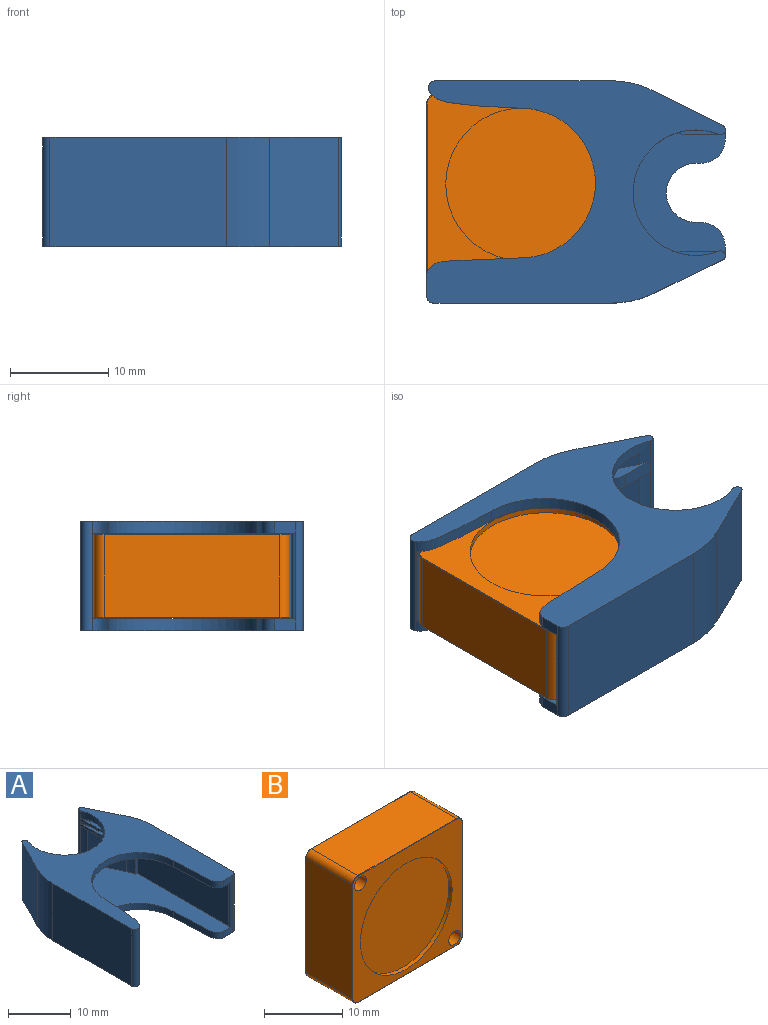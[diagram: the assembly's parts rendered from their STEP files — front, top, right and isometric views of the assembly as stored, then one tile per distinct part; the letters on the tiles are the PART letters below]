
ASSEMBLY  parts=2 mates=1
PART A: 64 faces, bbox 22.6x30.4x11.1 mm
  f0: plane 6.9x5.9mm, normal (-0.9,-0.44,0), area 45.2mm2, adj f2,f9,f31,f49
  f1: plane 5.9x2.86mm, normal (-0.9,-0.44,0), area 2mm2, adj f5,f15,f31,f55
  f2: cylinder r=6.38mm len=6.9mm, axis (0,0,1), area 8.8mm2, adj f0,f9,f42,f49
  f3: cylinder r=6.38mm len=1.23mm, axis (0,0,1), area 0.6mm2, adj f30,f42,f51,f53
  f4: plane 5.94x2.98mm, normal (0.89,-0.45,0), area 8.6mm2, adj f5,f15,f32,f47
  f5: cylinder r=6.38mm len=12.75mm, axis (0,0,1), area 31.7mm2, adj f1,f4,f8,f15,f40,f42,f47,f55
  f6: plane 2.16x1.2mm, normal (0,-1,0), area 2.6mm2, adj f8,f15,f24,f43
  f7: plane 1.2x0.88mm, normal (0,1,0), area 1.1mm2, adj f9,f10,f38,f39
  f8: plane 30.35x22.6mm, normal (0,0,1), area 298.4mm2, adj f5,f6,f18,f19,f21,f22,f24,f25
  f9: plane 30.35x20.76mm, normal (0,0,1), area 291.2mm2, adj f0,f2,f7,f11,f12,f13,f14,f16
  f10: plane 30.35x22.6mm, normal (0,0,-1), area 364.4mm2, adj f7,f11,f16,f18,f19,f20,f22,f23
  f11: plane 1.2x0.88mm, normal (0,1,0), area 1.1mm2, adj f9,f10,f37,f41
  f12: plane 8.7x0.32mm, normal (0,-1,0), area 2.8mm2, adj f9,f14,f15,f32
  f13: plane 8.7x0.3mm, normal (0,-1,0), area 2.6mm2, adj f9,f15,f17,f31
  f14: plane 20.66x8.7mm, normal (1,0,0), area 179.8mm2, adj f9,f12,f15,f22
  f15: plane 28.52x20.76mm, normal (0,0,-1), area 225.1mm2, adj f1,f4,f5,f6,f12,f13,f14,f17
  f16: plane 2.16x1.2mm, normal (0,-1,0), area 2.6mm2, adj f9,f10,f23,f43
  f17: plane 20.55x8.7mm, normal (-1,0,0), area 178.8mm2, adj f9,f13,f15,f45
  f18: plane 17.7x11.1mm, normal (-1,0,0), area 196.4mm2, adj f8,f10,f28,f44
  f19: plane 17.96x11.1mm, normal (1,0,0), area 199.3mm2, adj f8,f10,f27,f43
  f20: cylinder r=7.6mm len=15.2mm, axis (0,0,-1), area 28.7mm2, adj f9,f10,f22,f23
  f21: cylinder r=7.6mm len=15.2mm, axis (0,0,-1), area 28.7mm2, adj f8,f15,f22,f24
  f22: extruded ~11.1x9.24mm, area 23.5mm2, adj f8,f9,f10,f14,f15,f20,f21,f44
  f23: extruded ~9.55x1.69mm, area 12.2mm2, adj f9,f10,f16,f20
  f24: extruded ~9.55x1.69mm, area 12.2mm2, adj f6,f8,f15,f21
  f25: plane 11.1x6.96mm, normal (-0.89,0.45,0), area 86.4mm2, adj f8,f10,f28,f39
  f26: plane 11.1x7mm, normal (0.9,0.44,0), area 86.4mm2, adj f8,f10,f27,f41
  f27: cylinder r=10mm len=11.1mm, axis (0,0,1), area 50.1mm2, adj f8,f10,f19,f26
  f28: cylinder r=10mm len=11.1mm, axis (0,0,1), area 51.6mm2, adj f8,f10,f18,f25
  f29: plane 5.95x5.94mm, normal (0.89,-0.45,0), area 39.5mm2, adj f9,f32,f36,f46
  f30: plane 1.39x0.68mm, normal (-0.9,-0.44,0), area 0.8mm2, adj f3,f51,f53,f60
  f31: cylinder r=8.8mm len=8.7mm, axis (0,0,1), area 14.3mm2, adj f0,f1,f9,f13,f15,f58
  f32: cylinder r=8.8mm len=8.7mm, axis (0,0,1), area 14.7mm2, adj f4,f9,f12,f15,f29,f59
  f33: plane 1.2x0.5mm, normal (1,0,0), area 0.6mm2, adj f9,f10,f34,f38
  f34: cylinder r=3mm len=6mm, axis (0,0,-1), area 11.3mm2, adj f9,f10,f33,f35
  f35: plane 1.2x0.5mm, normal (-1,0,0), area 0.6mm2, adj f9,f10,f34,f37
  f36: cylinder r=6.38mm len=5.95mm, axis (0,0,1), area 7.1mm2, adj f9,f29,f40,f46
  f37: cylinder r=2.5mm len=2.5mm, axis (0,0,-1), area 4.7mm2, adj f9,f10,f11,f35
  f38: cylinder r=2.5mm len=2.5mm, axis (0,0,1), area 4.7mm2, adj f7,f9,f10,f33
  f39: cylinder r=0.5mm len=11.1mm, axis (0,0,1), area 6mm2, adj f7,f8,f9,f10,f25,f40
  f40: cylinder r=0.5mm len=9.9mm, axis (0,0,1), area 9.5mm2, adj f5,f8,f9,f36,f39,f48
  f41: cylinder r=0.5mm len=11.1mm, axis (0,0,-1), area 6.1mm2, adj f8,f9,f10,f11,f26,f42
  f42: cylinder r=0.5mm len=9.9mm, axis (0,0,1), area 9.5mm2, adj f2,f3,f5,f8,f9,f41,f50,f54
  f43: cylinder r=0.75mm len=11.1mm, axis (0,0,1), area 13.1mm2, adj f6,f8,f10,f16,f19,f45
  f44: cylinder r=0.75mm len=11.1mm, axis (0,0,-1), area 17.9mm2, adj f8,f10,f18,f22
  f45: cylinder r=0.45mm len=8.7mm, axis (0,0,-1), area 6.1mm2, adj f9,f15,f17,f43
  f46: plane 7.09x3.31mm, normal (0,0,-1), area 7.2mm2, adj f29,f36,f48,f56,f59,f63
  f47: plane 7.09x3.31mm, normal (0,0,1), area 7.2mm2, adj f4,f5,f48,f56,f59,f63
  f48: plane 3.49x1.45mm, normal (1,0,0), area 5.1mm2, adj f40,f46,f47,f63
  f49: plane 7.13x3.21mm, normal (0,0,-1), area 7mm2, adj f0,f2,f50,f57,f58,f62
  f50: plane 3.51x0.5mm, normal (-1,0,0), area 1.8mm2, adj f42,f49,f51,f62
  f51: plane 6.02x1.5mm, normal (0,0,1), area 4.7mm2, adj f3,f30,f50,f52,f57,f60,f62
  f52: plane 1.33x0.5mm, normal (-1,0,0), area 0.7mm2, adj f51,f53,f57,f60
  f53: plane 6.02x1.5mm, normal (0,0,-1), area 4.7mm2, adj f3,f30,f52,f54,f57,f60,f61
  f54: plane 3.51x0.5mm, normal (-1,0,0), area 1.8mm2, adj f42,f53,f55,f61
  f55: plane 7.13x3.21mm, normal (0,0,1), area 7mm2, adj f1,f5,f54,f57,f58,f61
  f56: plane 1.45x0.75mm, normal (0.71,-0.71,0), area 1.5mm2, adj f46,f47,f59,f63
  f57: plane 1.5x0.8mm, normal (-0.71,-0.71,0), area 1.1mm2, adj f49,f51,f52,f53,f55,f58,f61,f62
  f58: cylinder r=4.73mm len=1.71mm, axis (0,0,1), area 3.1mm2, adj f31,f49,f55,f57
  f59: cylinder r=4.73mm len=1.83mm, axis (0,0,1), area 3.2mm2, adj f32,f46,f47,f56
  f60: cylinder r=4.73mm len=2.07mm, axis (0,0,-1), area 1.1mm2, adj f30,f51,f52,f53
  f61: cylinder r=2.43mm len=1.72mm, axis (0,0,-1), area 1mm2, adj f53,f54,f55,f57
  f62: cylinder r=2.43mm len=1.72mm, axis (0,0,-1), area 1mm2, adj f49,f50,f51,f57
  f63: cylinder r=2.43mm len=1.72mm, axis (0,0,1), area 2.8mm2, adj f46,f47,f48,f56
PART B: 37 faces, bbox 20x8.5x20 mm
  f0: plane 17.85x8.4mm, normal (1,0,0), area 44.9mm2, adj f10,f11,f12,f13,f18,f19,f22,f31
  f1: plane 17.85x8.4mm, normal (0,0,-1), area 149.9mm2, adj f17,f18,f23,f30
  f2: plane 17.85x8.4mm, normal (-1,0,0), area 149.9mm2, adj f17,f20,f27,f34
  f3: plane 17.85x8.4mm, normal (0,0,1), area 149.9mm2, adj f19,f20,f26,f35
  f4: plane 19.75x19.75mm, normal (0,1,0), area 193.7mm2, adj f6,f15,f16,f29,f30,f31,f32,f33
  f5: plane 19.75x19.75mm, normal (0,-1,0), area 165.9mm2, adj f8,f15,f16,f21,f22,f23,f24,f25
  f6: cylinder r=7.75mm len=15.5mm, axis (0,1,0), area 29.2mm2, adj f4,f7
  f7: plane 15.5x15.5mm, normal (0,1,0), area 188.7mm2, adj f6
  f8: cylinder r=8.3mm len=16.6mm, axis (0,-1,0), area 31.3mm2, adj f5,f9
  f9: plane 16.6x16.6mm, normal (0,-1,0), area 216.4mm2, adj f8
  f10: plane 7x0.6mm, normal (0,0,-1), area 4.2mm2, adj f0,f11,f13,f14
  f11: plane 15x0.6mm, normal (0,-1,0), area 9mm2, adj f0,f10,f12,f14
  f12: plane 7x0.6mm, normal (0,0,1), area 4.2mm2, adj f0,f11,f13,f14
  f13: plane 15x0.6mm, normal (0,1,0), area 9mm2, adj f0,f10,f12,f14
  f14: plane 15x7mm, normal (1,0,0), area 105mm2, adj f10,f11,f12,f13
  f15: cylinder r=1.05mm len=8.5mm, axis (0,1,0), area 56.1mm2, adj f4,f5
  f16: cylinder r=1.05mm len=8.5mm, axis (0,1,0), area 56.1mm2, adj f4,f5
  f17: cylinder r=1mm len=8.4mm, axis (0,-1,0), area 13.2mm2, adj f1,f2,f25,f32
  f18: cylinder r=1mm len=8.4mm, axis (0,-1,0), area 13.2mm2, adj f0,f1,f21,f29
  f19: cylinder r=1mm len=8.4mm, axis (0,-1,0), area 13.2mm2, adj f0,f3,f24,f33
  f20: cylinder r=1mm len=8.4mm, axis (0,-1,0), area 13.2mm2, adj f2,f3,f28,f36
  f21: torus R=0.95mm, axis (0,-1,0), area 0.1mm2, adj f5,f18,f22,f23
  f22: cylinder r=0.05mm len=17.85mm, axis (0,0,1), area 1.4mm2, adj f0,f5,f21,f24
  f23: cylinder r=0.05mm len=17.85mm, axis (1,0,0), area 1.4mm2, adj f1,f5,f21,f25
  f24: torus R=0.95mm, axis (0,-1,0), area 0.1mm2, adj f5,f19,f22,f26
  f25: torus R=0.95mm, axis (0,-1,0), area 0.1mm2, adj f5,f17,f23,f27
  f26: cylinder r=0.05mm len=17.85mm, axis (-1,0,0), area 1.4mm2, adj f3,f5,f24,f28
  f27: cylinder r=0.05mm len=17.85mm, axis (0,0,-1), area 1.4mm2, adj f2,f5,f25,f28
  f28: torus R=0.95mm, axis (0,-1,0), area 0.1mm2, adj f5,f20,f26,f27
  f29: torus R=0.95mm, axis (0,-1,0), area 0.1mm2, adj f4,f18,f30,f31
  f30: cylinder r=0.05mm len=17.85mm, axis (-1,0,0), area 1.4mm2, adj f1,f4,f29,f32
  f31: cylinder r=0.05mm len=17.85mm, axis (0,0,-1), area 1.4mm2, adj f0,f4,f29,f33
  f32: torus R=0.95mm, axis (0,-1,0), area 0.1mm2, adj f4,f17,f30,f34
  f33: torus R=0.95mm, axis (0,-1,0), area 0.1mm2, adj f4,f19,f31,f35
  f34: cylinder r=0.05mm len=17.85mm, axis (0,0,1), area 1.4mm2, adj f2,f4,f32,f36
  f35: cylinder r=0.05mm len=17.85mm, axis (1,0,0), area 1.4mm2, adj f3,f4,f33,f36
  f36: torus R=0.95mm, axis (0,-1,0), area 0.1mm2, adj f4,f20,f34,f35
PLACE A rot(axis=(0,0,-1),90deg) t=(-27.35,11.39,21.52)mm
PLACE B rot(axis=(1,0,0),90deg) t=(-17.43,0.09,27.07)mm
MATE planar B.f2 <-> A.f16  axis (-1,0,0) through (-27.35,0.09,27.07)mm
